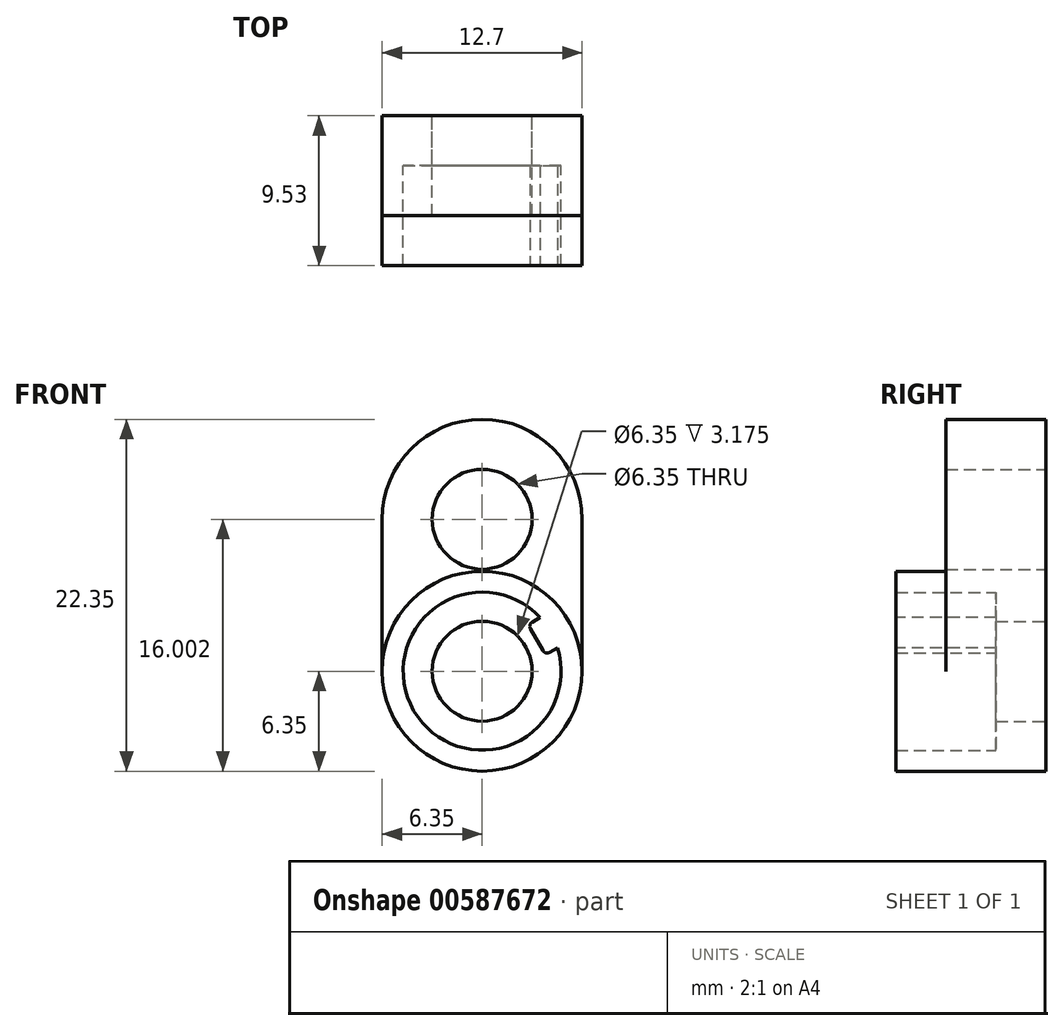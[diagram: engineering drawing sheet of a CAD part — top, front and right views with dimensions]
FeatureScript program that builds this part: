
annotation { "Feature Type Name" : "Feature", "Feature Type Description" : "" }
export const myFeature = defineFeature(function(context is Context, id is Id, definition is map)
    precondition{}
    {
        {
            var Q0;
            Q0=qCreatedBy(makeId("Front.planeOp"),FACE);
            var sketch = newSketch(context, id + "F0", { "sketchPlane" : qUnion([Q0])});
            skCircle(sketch, "E0", {"center": v(0, 0) * mm, "radius": 3.18 * mm});
            skCircle(sketch, "E1", {"center": v(0, 0) * mm, "radius": 6.35 * mm});
            skSolve(sketch);
        }
        {
            var Q0;
            Q0=qSketchRegion(id+"F0",true);
            extrude(context, id + "F1", {"entities" : qUnion([Q0]), "depth" : 3.17 * mm, "offsetDistance" : 25.4 * mm});
        }
        {
            var Q0;
            Q0=makeQuery(id+"F1.opExtrude","CAP_FACE",FACE,{"disambiguationData":[OSD([sQuery(id+"F0.wireOp",EDGE,"E0"),sQuery(id+"F0.wireOp",EDGE,"E1")])],"isStart":false});
            var sketch = newSketch(context, id + "F2", { "sketchPlane" : qUnion([Q0])});
            skCircle(sketch, "E2", {"center": v(0, 0) * mm, "radius": 5.02 * mm});
            skCircle(sketch, "E3.0", {"center": v(0, 0) * mm, "radius": 6.35 * mm});
            skSolve(sketch);
        }
        {
            var Q0;
            Q0=qSketchRegion(id+"F2",true);
            extrude(context, id + "F3", {"entities" : qUnion([Q0]), "operationType" : NewBodyOperationType.ADD, "depth" : 6.35 * mm, "offsetDistance" : 25.4 * mm});
        }
        {
            var Q0;
            Q0=makeQuery(id+"F1.opExtrude","CAP_FACE",FACE,{"disambiguationData":[OSD([sQuery(id+"F0.wireOp",EDGE,"E0"),sQuery(id+"F0.wireOp",EDGE,"E1")])],"isStart":true});
            var sketch = newSketch(context, id + "F4", { "sketchPlane" : qUnion([Q0])});
            skLineSegment(sketch, "E4", {"start": v(0, 0) * mm, "end": v(0, 9.65) * mm, "construction": true});
            skCircle(sketch, "E5", {"center": v(0, 9.65) * mm, "radius": 3.18 * mm});
            skCircle(sketch, "E6.0", {"center": v(0, 0) * mm, "radius": 6.35 * mm});
            skLineSegment(sketch, "E7", {"start": v(-6.35, 0) * mm, "end": v(-6.35, 9.65) * mm});
            skLineSegment(sketch, "E8", {"start": v(6.35, 0) * mm, "end": v(6.35, 9.65) * mm});
            skLineSegment(sketch, "E9", {"start": v(0, 9.65) * mm, "end": v(0, 9.65) * mm});
            skCircle(sketch, "E10", {"center": v(0, 9.65) * mm, "radius": 6.35 * mm});
            skLineSegment(sketch, "E11", {"start": v(-6.35, 9.65) * mm, "end": v(0, 9.65) * mm, "construction": true});
            skLineSegment(sketch, "E12", {"start": v(0, 9.65) * mm, "end": v(6.35, 9.65) * mm, "construction": true});
            skSolve(sketch);
        }
        {
            var Q0;
            {var subQ1=sQuery(id+"F4.wireOp",EDGE,"gx27LyLz-Ukwh-S3wJ-jbhg-FnkPYNk82Kv1");Q0=makeQuery(id+"F4.imprint","IMPRINT",FACE,{"disambiguationData":[TD([[makeQuery(id+"F4.imprint","IMPRINT",EDGE,{"derivedFrom":subQ1}),-1.0]])]});}
            var Q1;
            Q1=makeQuery(id+"F4.imprint","IMPRINT",FACE,{"disambiguationData":[TD([[makeQuery(id+"F4.imprint","IMPRINT",EDGE,{"derivedFrom":sQuery(id+"F4.wireOp",EDGE,"E5")}),-1.0]])]});
            var Q2;
            {var subQ0=sQuery(id+"F4.wireOp",EDGE,"E7");Q2=makeQuery(id+"F4.imprint","IMPRINT",FACE,{"disambiguationData":[TD([[makeQuery(id+"F4.imprint","IMPRINT",EDGE,{"derivedFrom":subQ0}),-1.0]])]});}
            var Q3;
            {var subQ0=sQuery(id+"F4.wireOp",EDGE,"E8");Q3=makeQuery(id+"F4.imprint","IMPRINT",FACE,{"disambiguationData":[TD([[makeQuery(id+"F4.imprint","IMPRINT",EDGE,{"derivedFrom":subQ0}),1.0]])]});}
            extrude(context, id + "F5", {"entities" : qUnion([Q0, Q1, Q2, Q3]), "operationType" : NewBodyOperationType.ADD, "oppositeDirection" : true, "depth" : 6.35 * mm, "offsetDistance" : 25.4 * mm});
        }
        {
            var Q0;
            Q0=makeQuery(id+"F3.opExtrude","CAP_FACE",FACE,{"disambiguationData":[OSD([sQuery(id+"F2.wireOp",EDGE,"E2"),sQuery(id+"F2.wireOp",EDGE,"E3.0")])],"isStart":false});
            var sketch = newSketch(context, id + "F6", { "sketchPlane" : qUnion([Q0])});
            skLineSegment(sketch, "E13", {"start": v(0, 0) * mm, "end": v(4.34, 2.5) * mm, "construction": true});
            skArc(sketch, "E14.0", {"start": v(4.8, 1.49) * mm, "mid": v(4.34, 2.5) * mm, "end": v(3.69, 3.4) * mm});
            skLineSegment(sketch, "E15", {"start": v(4.02, 1.04) * mm, "end": v(4.8, 1.49) * mm});
            skLineSegment(sketch, "E16", {"start": v(2.91, 2.96) * mm, "end": v(3.69, 3.4) * mm});
            skLineSegment(sketch, "E17", {"start": v(4.02, 1.04) * mm, "end": v(2.91, 2.96) * mm});
            skLineSegment(sketch, "E18", {"start": v(4.8, 1.49) * mm, "end": v(4.24, 2.45) * mm, "construction": true});
            skLineSegment(sketch, "E19", {"start": v(4.24, 2.45) * mm, "end": v(3.69, 3.4) * mm, "construction": true});
            skLineSegment(sketch, "E20", {"start": v(0, 0) * mm, "end": v(0, -5.02) * mm, "construction": true});
            skSolve(sketch);
        }
        {
            var Q0;
            Q0=qSketchRegion(id+"F6",true);
            var Q1;
            Q1=makeQuery(id+"F1.opExtrude","CAP_FACE",FACE,{"disambiguationData":[OSD([sQuery(id+"F0.wireOp",EDGE,"E0"),sQuery(id+"F0.wireOp",EDGE,"E1")])],"isStart":false});
            extrude(context, id + "F7", {"entities" : qUnion([Q0]), "operationType" : NewBodyOperationType.ADD, "endBound" : BoundingType.UP_TO_SURFACE, "oppositeDirection" : true, "depth" : 25.4 * mm, "endBoundEntityFace" : qUnion([Q1]), "offsetDistance" : 25.4 * mm});
        }
        {
            var Q0;
            Q0=makeQuery(id+"F7.opExtrude","SWEPT_EDGE",EDGE,{"disambiguationData":[OSD([sQuery(id+"F6.wireOp",EDGE,"E16"),sQuery(id+"F6.wireOp",EDGE,"E17")])]});
            var Q1;
            Q1=makeQuery(id+"F7.opExtrude","SWEPT_EDGE",EDGE,{"disambiguationData":[OSD([sQuery(id+"F6.wireOp",EDGE,"E15"),sQuery(id+"F6.wireOp",EDGE,"E17")])]});
            fillet(context, id + "F8", {"entities" : qUnion([Q0, Q1]), "radius" : 0.3 * mm, "tangentPropagation" : true, "allowEdgeOverflow" : false});
        }
    });
